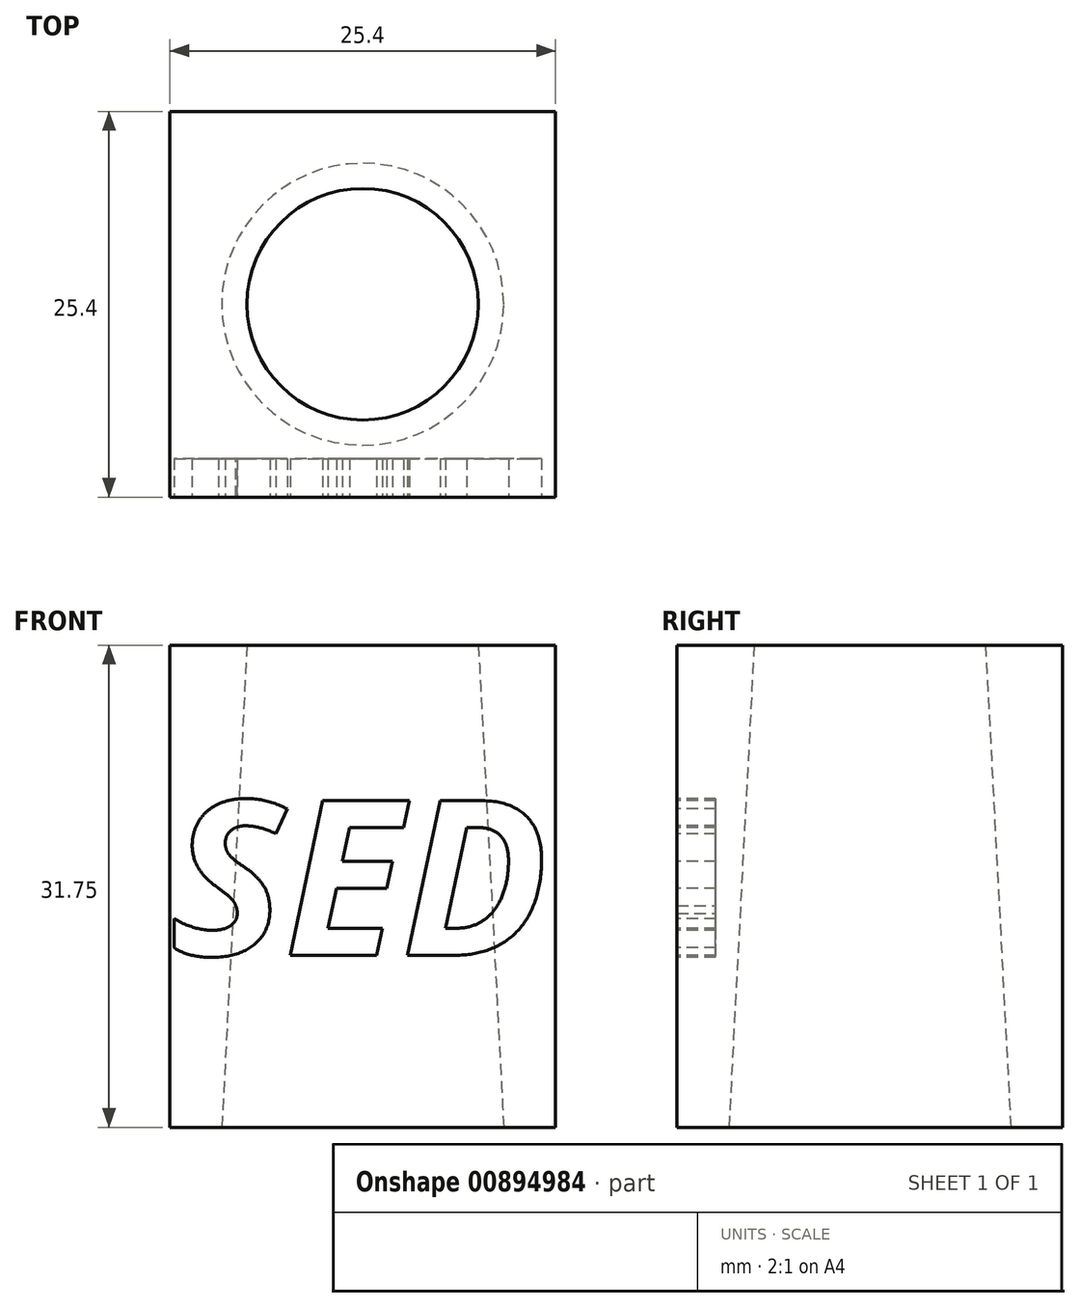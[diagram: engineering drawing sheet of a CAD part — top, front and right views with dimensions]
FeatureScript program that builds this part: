
annotation { "Feature Type Name" : "Feature", "Feature Type Description" : "" }
export const myFeature = defineFeature(function(context is Context, id is Id, definition is map)
    precondition{}
    {
        {
            var Q0;
            Q0=qCreatedBy(makeId("Top.planeOp"),FACE);
            var sketch = newSketch(context, id + "F0", { "sketchPlane" : qUnion([Q0])});
            skLineSegment(sketch, "E0.bottom", {"start": v(0, 0) * mm, "end": v(25.4, 0) * mm});
            skLineSegment(sketch, "E0.top", {"start": v(0, 25.4) * mm, "end": v(25.4, 25.4) * mm});
            skLineSegment(sketch, "E0.left", {"start": v(0, 0) * mm, "end": v(0, 25.4) * mm});
            skLineSegment(sketch, "E0.right", {"start": v(25.4, 0) * mm, "end": v(25.4, 25.4) * mm});
            skSolve(sketch);
        }
        {
            var Q0;
            Q0 = qSketchRegion(id + "F0", true);
            extrude(context, id + "F1", {"entities" : qUnion([Q0]), "depth" : 31.75 * mm, "offsetDistance" : 25.4 * mm});
        }
        {
            var Q0;
            Q0=makeQuery(id+"F1.opExtrude","CAP_FACE",FACE,{"disambiguationData":[OSD([sQuery(id+"F0.wireOp",EDGE,"E0.bottom"),sQuery(id+"F0.wireOp",EDGE,"E0.top"),sQuery(id+"F0.wireOp",EDGE,"E0.left"),sQuery(id+"F0.wireOp",EDGE,"E0.right")])],"isStart":false});
            var sketch = newSketch(context, id + "F2", { "sketchPlane" : qUnion([Q0])});
            skCircle(sketch, "E1", {"center": v(12.7, 12.7) * mm, "radius": 7.62 * mm});
            skPoint(sketch, "E1.centerSnap0", {"position": v(25.4, 12.7) * mm});
            skSolve(sketch);
        }
        {
            var Q0;
            Q0 = qSketchRegion(id + "F2", true);
            extrude(context, id + "F3", {"entities" : qUnion([Q0]), "operationType" : NewBodyOperationType.REMOVE, "oppositeDirection" : true, "depth" : 31.75 * mm, "offsetDistance" : 25.4 * mm, "hasDraft" : true, "draftAngle" : 3 * degree});
        }
        {
            var Q0;
            Q0=makeQuery(id+"F1.opExtrude","SWEPT_FACE",FACE,{"disambiguationData":[OSD([sQuery(id+"F0.wireOp",EDGE,"E0.bottom")])]});
            var sketch = newSketch(context, id + "F4", { "sketchPlane" : qUnion([Q0])});
            skText(sketch, "E2", { "text": "SED", "fontName": "OpenSans-BoldItalic.ttf"});
            const initialGuessF4  = {"E2": [0, 0.01133, 1, 0, 0.01026]};
            skSetInitialGuess(sketch, initialGuessF4);
            skSolve(sketch);
        }
        {
            var Q0;
            Q0 = qSketchRegion(id + "F4", true);
            extrude(context, id + "F5", {"entities" : qUnion([Q0]), "operationType" : NewBodyOperationType.REMOVE, "oppositeDirection" : true, "depth" : 2.54 * mm, "offsetDistance" : 25.4 * mm});
        }
    });
